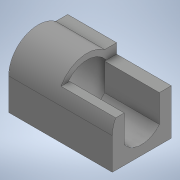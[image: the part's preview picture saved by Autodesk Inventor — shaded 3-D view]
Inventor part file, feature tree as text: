
AUTODESK INVENTOR PART (.ipt)
format: ipt  version: 2020 (Build 240168000, 168)  size: 608,768 bytes
history: native  units: mm
features: extrude x24, sketch x24, projected_geometry x10, chamfer x6, plane x3, mirror x2
ambient origin geometry x8: Origin, YZ Plane, XZ Plane, XY Plane, X Axis, Y Axis, Z Axis, Center Point
bodies: Solid1 (feature_tree)
feature tree (69):
  extrude  "Extrusion1"  Depth=120.0mm
  extrude  "Extrusion2"  TaperAngle=0.0deg  [1 undecoded]
  plane  "Work Plane2"
  extrude  "Extrusion6"  Depth=10.0mm
  plane  "Work Plane4"
  plane  "Work Plane5"
  extrude  "Extrusion7"  TaperAngle=0.0deg  [1 undecoded]
  extrude  "Extrusion8"  Depth=83.204mm TaperAngle=0.0deg
  chamfer  "Chamfer1"  Distance=20.747mm
  chamfer  "Chamfer2"  Distance=27.254mm
  chamfer  "Chamfer3"  Distance=2.0mm Angle=45.0deg
  chamfer  "Chamfer4"  Distance=6.0mm Angle=45.0deg
  chamfer  "Chamfer6"  [1 undecoded]
  extrude  "Extrusion9"  TaperAngle=0.0deg  [1 undecoded]
  extrude  "Extrusion10"  Depth=6.5mm
  extrude  "Extrusion11"  Depth=15.0mm
  extrude  "Extrusion12"  Depth=4.5mm
  mirror  "Mirror2"
  extrude  "WeaponMountSlot"  Depth=10.0mm TaperAngle=0.0deg
  chamfer  "Chamfer7"  Distance=55.8mm
  extrude  "Extrusion14"  Depth=19.0mm TaperAngle=45.0deg
  extrude  "Extrusion15"  Depth=19.0mm
  extrude  "Extrusion16"  Depth=19.0mm
  extrude  "Extrusion17"  TaperAngle=0.0deg  [1 undecoded]
  extrude  "WeaponMountHoles"  Depth=19.0mm
  extrude  "Extrusion19"  Depth=19.0mm
  extrude  "Extrusion20"  Depth=19.0mm
  extrude  "Extrusion21"  Depth=19.0mm
  mirror  "Mirror3"
  extrude  "Extrusion22"  Depth=19.0mm
  extrude  "Extrusion23"  TaperAngle=0.0deg  [1 undecoded]
  extrude  "Extrusion24"  Depth=19.0mm
  extrude  "Extrusion25"  Depth=19.0mm
  extrude  "Extrusion26"  Depth=19.0mm
  extrude  "Extrusion27"  Depth=19.0mm
  sketch  "Sketch1"  dims[d0=180.0mm d1=120.0mm]
  sketch  "Sketch3"  dims[d2=30.0mm d3=0.0mm]
  sketch  "Sketch7"  dims[d4=100.8mm d5=10.0mm]
  projected_geometry  "Projected Loop3"
  sketch  "Sketch9"  dims[d6=10.0mm d7=0.0mm d8=0.0mm]
  sketch  "Sketch10"  dims[d10=45.0deg d18=83.204mm d19=0.0mm d20=20.747mm d21=0.0mm d22=27.254mm d23=0.0mm]
  sketch  "Sketch11"  dims[d24=10.0mm d25=2.0mm d26=45.0deg]
  projected_geometry  "Projected Loop4"
  sketch  "Sketch12"  dims[d27=3.0mm d28=6.0mm d29=45.0deg]
  projected_geometry  "Projected Loop8"
  sketch  "Sketch16"  dims[d30=24.0mm]
  sketch  "Sketch17"  dims[d31=3.0mm]
  sketch  "Sketch18"  dims[d32=45.0deg]
  sketch  "Sketch19"  dims[d33=3.0mm]
  sketch  "Sketch20"  dims[d34=6.0mm]
  projected_geometry  "Projected Loop9"
  projected_geometry  "Projected Loop10"
  projected_geometry  "Projected Loop11"
  projected_geometry  "Projected Loop12"
  sketch  "Sketch21"  dims[d35=45.0deg]
  sketch  "Sketch22"  dims[d39=24.0mm]
  sketch  "Sketch23"  dims[d40=3.0mm]
  sketch  "Sketch24"  dims[d41=45.0deg]
  sketch  "Sketch25"  dims[d45=17.7mm]
  sketch  "Sketch26"  dims[d46=44.25mm d47=0.0mm d48=0.0mm]
  projected_geometry  "Projected Loop13"
  sketch  "Sketch27"  dims[d52=27.0mm d53=0.0mm]
  projected_geometry  "Projected Loop14"
  sketch  "Sketch29"  dims[d58=6.0mm d64=6.5mm]
  sketch  "Sketch30"  dims[d65=16.25mm d66=15.0mm]
  sketch  "Sketch31"  dims[d67=157.438mm d68=0.0mm d69=4.5mm]
  sketch  "Sketch32"  dims[d70=173.156mm d71=0.0mm d72=10.0mm d73=0.0mm]
  sketch  "Sketch33"  dims[d75=37.4mm d76=55.8mm d77=5.0mm d78=2.0mm d79=45.0deg d80=8.0mm d81=26.0mm d82=0.0mm d83=3.75mm d84=3.75mm d85=3.75mm d86=3.75mm d87=7.0mm d88=0.0mm d90=6.0mm d91=4.0mm d92=15.0mm d93=23.0mm d94=7.0mm d95=0.0mm d96=4.0mm d97=15.0mm d98=23.0mm d99=7.0mm d100=0.0mm d101=3.0mm d102=60.0mm d103=3.1mm d104=3.1mm d105=3.1mm d106=3.1mm d107=10.0mm d108=9.4mm d109=9.4mm d110=64.0mm d111=64.0mm d112=9.4mm d113=9.4mm d114=10.0mm d115=27.0mm d116=0.0mm d117=6.1mm d118=0.0mm d119=-7.853982mm d120=16.5mm d121=16.25mm d122=15.0mm d123=2.0mm d124=20.5mm d125=17.0mm d126=0.0mm d127=15.5mm d128=12.2mm d129=19.0mm d130=0.0mm d131=45.0deg d133=19.0mm d134=0.0mm d135=8.0mm d137=6.1mm d138=0.0mm d139=0.0mm d140=0.0mm d141=0.0mm d142=115.01mm d143=0.0mm d144=76.966mm d145=0.0mm d146=4.0mm d147=0.0mm]
  projected_geometry  "Projected Loop15"
note: 6 required parameter values undecoded (feature->parameter linkage not recoverable at this tier; creation-order binding heuristic only, values carry confidence <= 0.55)
